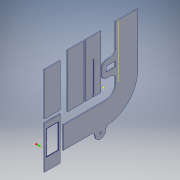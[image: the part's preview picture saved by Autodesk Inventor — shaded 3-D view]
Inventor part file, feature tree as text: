
AUTODESK INVENTOR PART (.ipt)
format: ipt  version: 2016 (Build 200138000, 138)  size: 487,936 bytes
history: native  units: in
note: dims shown in document units (in); Inventor stores cm internally (conversion verified against a paired STEP export)
features: sketch x8, extrude x6, direct_edit x2, pattern_linear x2, fillet x2, move_body x2
ambient origin geometry x8: Origin, YZ Plane, XZ Plane, XY Plane, X Axis, Y Axis, Z Axis, Center Point
bodies: Solid1 (feature_tree)
feature tree (22):
  sketch  "Sketch1"  dims[d0=0.0591in d1=0.0in d2=0.1181in d3=0.0in]
  extrude  "Extrusion1"  Depth=0.1181in TaperAngle=0.0deg
  extrude  "Extrusion2"  TaperAngle=0.0deg  [1 undecoded]
  direct_edit  "Direct Edit1"
  direct_edit  "Direct Edit2"
  sketch  "Sketch4"  dims[d12=0.0787in d13=0.0in d14=0.7874in d16=1.9291in]
  extrude  "Extrusion3"  Depth=1.752in
  pattern_linear  "Rectangular Pattern1"  Count1=2 Spacing1=1.9291in
  extrude  "Extrusion4"  Depth=0.1969in
  fillet  "Fillet1"  [1 undecoded]
  extrude  "Extrusion5"  Depth=0.0787in
  pattern_linear  "Rectangular Pattern2"  Count1=12  [1 undecoded]
  extrude  "Extrusion6"  Depth=0.0787in TaperAngle=0.0deg
  sketch  "Sketch2"  dims[d4=0.0in d5=0.0in d6=-0.0394in d7=0.0in d8=0.0in d9=-0.0197in]
  sketch  "Sketch3"  dims[d10=5.9055in d11=1.752in]
  sketch  "Sketch5"  dims[d17=3.5433in d18=0.1969in d19=0.0in d20=0.0in]
  sketch  "Sketch6"  dims[d21=0.0984in d22=0.0787in]
  sketch  "Sketch7"  dims[d23=1.752in d24=4.7244in]
  sketch  "Sketch8"  dims[d25=0.3937in d26=0.0787in d27=0.0in d28=0.7874in d30=5.1181in d31=1.378in d32=2.7559in d33=0.6299in d34=0.0787in d35=0.0in]
  fillet  "Fillet2"  Radius=0.7874in
  move_body  "Move1"
  move_body  "Move2"
note: 3 required parameter values undecoded (feature->parameter linkage not recoverable at this tier; creation-order binding heuristic only, values carry confidence <= 0.55)
